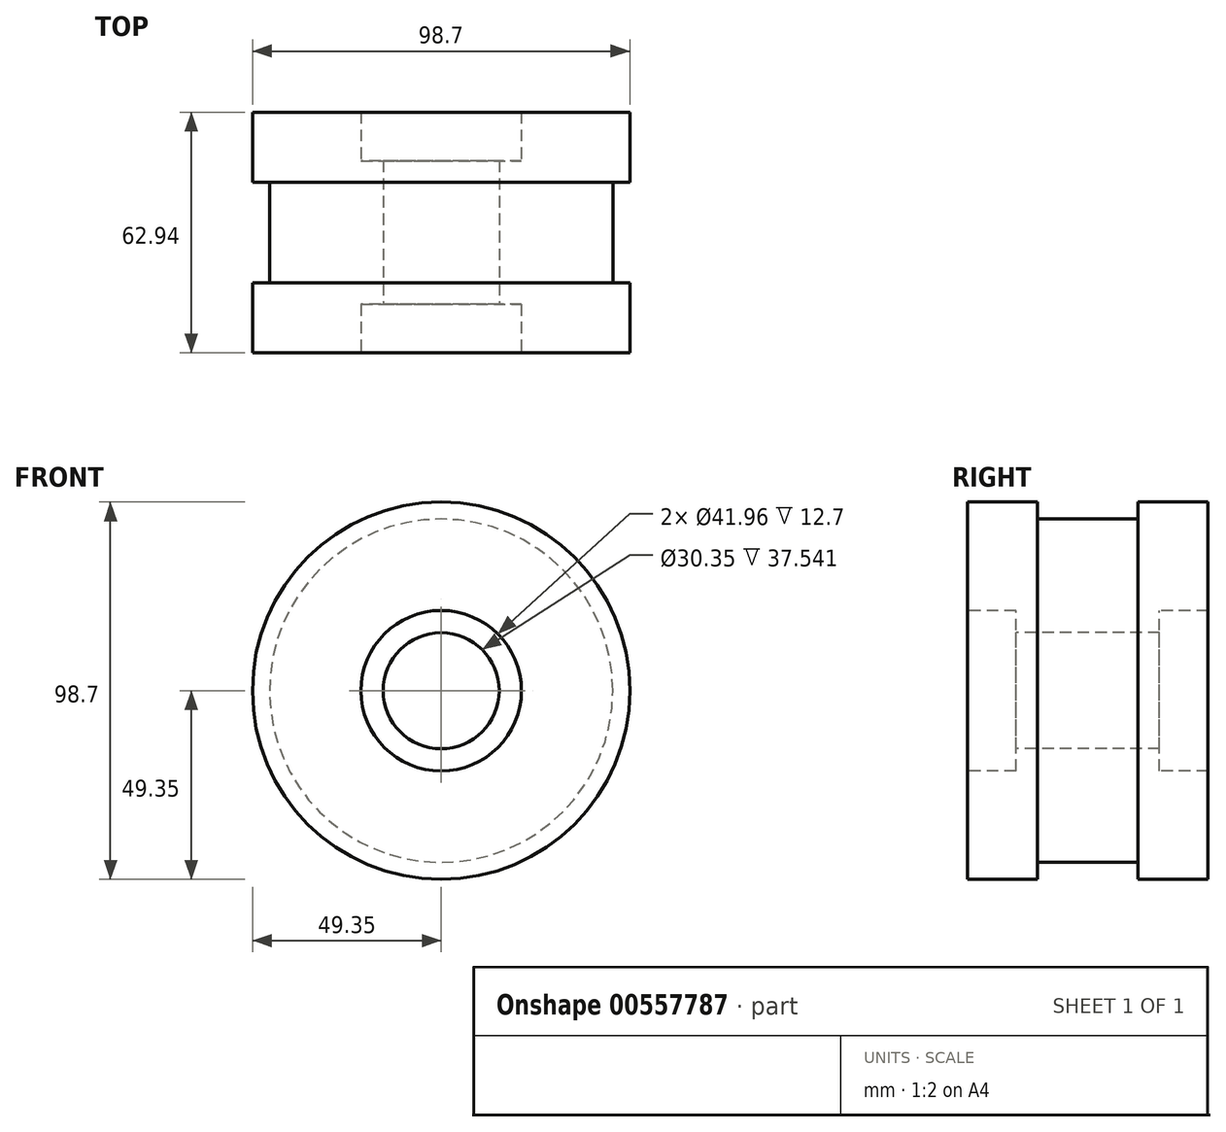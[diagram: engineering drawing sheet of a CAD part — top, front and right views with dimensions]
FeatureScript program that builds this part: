
annotation { "Feature Type Name" : "Feature", "Feature Type Description" : "" }
export const myFeature = defineFeature(function(context is Context, id is Id, definition is map)
    precondition{}
    {
        {
            var Q0;
            Q0=qCreatedBy(makeId("Right.planeOp"),FACE);
            var sketch = newSketch(context, id + "F0", { "sketchPlane" : qUnion([Q0])});
            skLineSegment(sketch, "E0", {"start": v(-35.21, 0) * mm, "end": v(33.24, 0) * mm, "construction": true});
            skLineSegment(sketch, "E1", {"start": v(0, 15.18) * mm, "end": v(-18.77, 15.18) * mm});
            skLineSegment(sketch, "E2", {"start": v(-18.77, 15.18) * mm, "end": v(-18.77, 20.98) * mm});
            skLineSegment(sketch, "E3", {"start": v(-18.77, 20.98) * mm, "end": v(-31.47, 20.98) * mm});
            skLineSegment(sketch, "E4", {"start": v(-31.47, 20.98) * mm, "end": v(-31.47, 49.35) * mm});
            skLineSegment(sketch, "E5", {"start": v(-31.47, 49.35) * mm, "end": v(-13.14, 49.35) * mm});
            skLineSegment(sketch, "E6", {"start": v(-13.14, 49.35) * mm, "end": v(-13.14, 44.88) * mm});
            skLineSegment(sketch, "E7", {"start": v(-13.14, 44.88) * mm, "end": v(13.14, 44.88) * mm});
            skLineSegment(sketch, "E8", {"start": v(0, 44.88) * mm, "end": v(0, 15.18) * mm, "construction": true});
            skLineSegment(sketch, "E9.MirrorCS", {"start": v(13.14, 49.35) * mm, "end": v(13.14, 44.88) * mm});
            skLineSegment(sketch, "E10.MirrorCS", {"start": v(31.47, 49.35) * mm, "end": v(13.14, 49.35) * mm});
            skLineSegment(sketch, "E11.MirrorCS", {"start": v(31.47, 20.98) * mm, "end": v(31.47, 49.35) * mm});
            skLineSegment(sketch, "E12.MirrorCS", {"start": v(18.77, 20.98) * mm, "end": v(31.47, 20.98) * mm});
            skLineSegment(sketch, "E13.MirrorCS", {"start": v(18.77, 15.18) * mm, "end": v(18.77, 20.98) * mm});
            skLineSegment(sketch, "E14.MirrorCS", {"start": v(0, 15.18) * mm, "end": v(18.77, 15.18) * mm});
            skPoint(sketch, "E15.orphan", {"position": v(0, 44.88) * mm});
            skSolve(sketch);
        }
        {
            var Q0;
            Q0=qSketchRegion(id+"F0",true);
            var Q1;
            Q1=sQuery(id+"F0.wireOp",EDGE,"E0");
            revolve(context, id + "F1", {"entities" : qUnion([Q0]), "axis" : qUnion([Q1]), "revolveType" : RevolveType.FULL});
        }
    });
